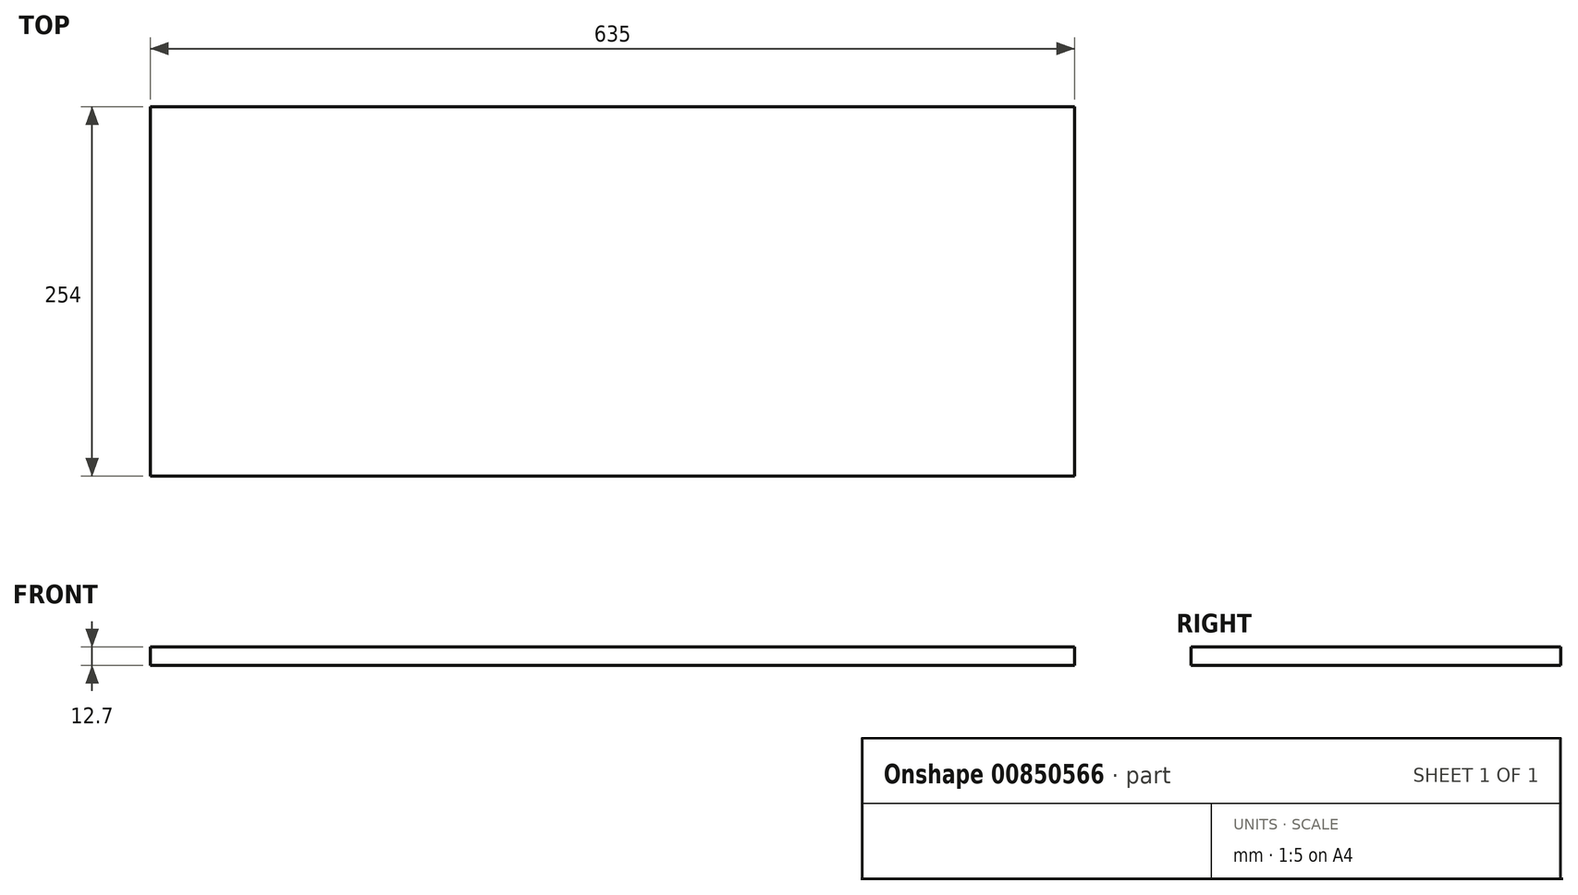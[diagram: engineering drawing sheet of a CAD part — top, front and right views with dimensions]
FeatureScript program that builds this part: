
annotation { "Feature Type Name" : "Feature", "Feature Type Description" : "" }
export const myFeature = defineFeature(function(context is Context, id is Id, definition is map)
    precondition{}
    {
        {
            var Q0;
            Q0=qCreatedBy(makeId("Top.planeOp"),FACE);
            var sketch = newSketch(context, id + "F0", { "sketchPlane" : qUnion([Q0])});
            skLineSegment(sketch, "E0.bottom", {"start": v(-624.12, 238.78) * mm, "end": v(10.88, 238.78) * mm});
            skLineSegment(sketch, "E0.top", {"start": v(-624.12, -15.22) * mm, "end": v(10.88, -15.22) * mm});
            skLineSegment(sketch, "E0.left", {"start": v(-624.12, 238.78) * mm, "end": v(-624.12, -15.22) * mm});
            skLineSegment(sketch, "E0.right", {"start": v(10.88, 238.78) * mm, "end": v(10.88, -15.22) * mm});
            skSolve(sketch);
        }
        {
            var Q0;
            Q0 = qSketchRegion(id + "F0", true);
            extrude(context, id + "F1", {"entities" : qUnion([Q0]), "depth" : 12.7 * mm, "offsetDistance" : 25.4 * mm});
        }
    });
